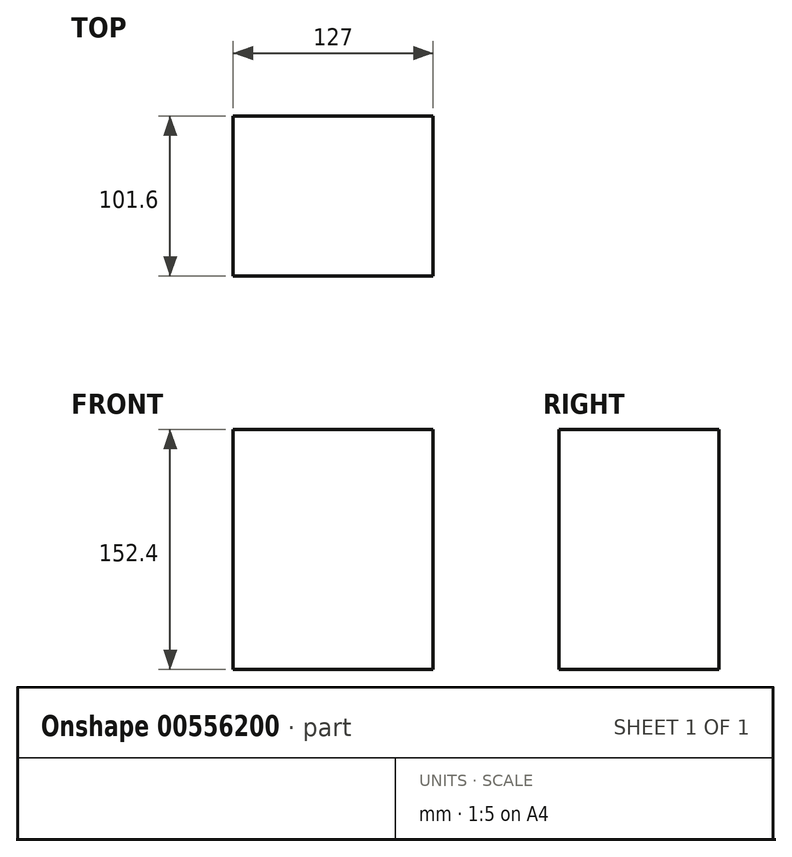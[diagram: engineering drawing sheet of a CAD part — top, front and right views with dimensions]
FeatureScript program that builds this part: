
annotation { "Feature Type Name" : "Feature", "Feature Type Description" : "" }
export const myFeature = defineFeature(function(context is Context, id is Id, definition is map)
    precondition{}
    {
        {
            var Q0;
            Q0=qCreatedBy(makeId("Top.planeOp"),FACE);
            var sketch = newSketch(context, id + "F0", { "sketchPlane" : qUnion([Q0])});
            skLineSegment(sketch, "E0.bottom", {"start": v(0, 0) * mm, "end": v(-127, 0) * mm});
            skLineSegment(sketch, "E0.top", {"start": v(0, 101.6) * mm, "end": v(-127, 101.6) * mm});
            skLineSegment(sketch, "E0.left", {"start": v(0, 0) * mm, "end": v(0, 101.6) * mm});
            skLineSegment(sketch, "E0.right", {"start": v(-127, 0) * mm, "end": v(-127, 101.6) * mm});
            skSolve(sketch);
        }
        {
            var Q0;
            Q0 = qSketchRegion(id + "F0", true);
            extrude(context, id + "F1", {"entities" : qUnion([Q0]), "depth" : 152.4 * mm, "offsetDistance" : 25.4 * mm});
        }
    });
